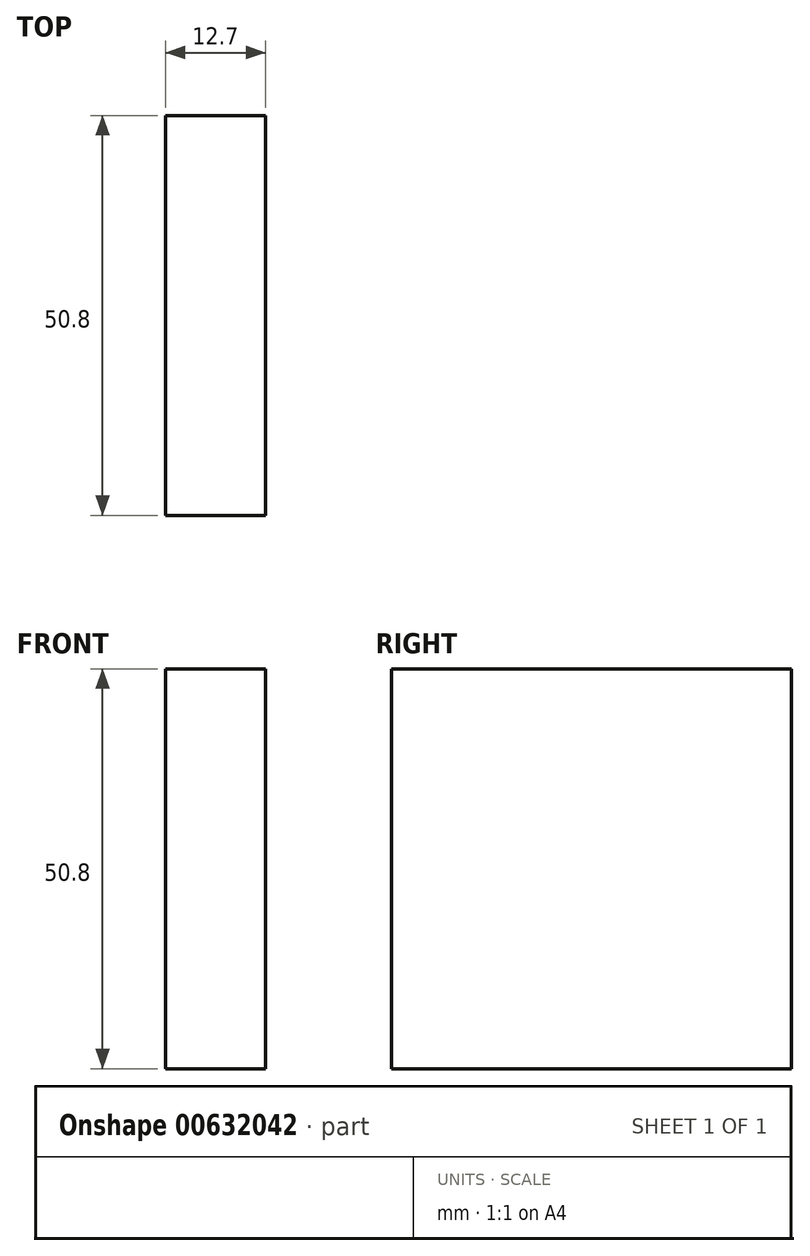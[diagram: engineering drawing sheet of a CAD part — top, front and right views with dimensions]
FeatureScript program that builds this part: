
annotation { "Feature Type Name" : "Feature", "Feature Type Description" : "" }
export const myFeature = defineFeature(function(context is Context, id is Id, definition is map)
    precondition{}
    {
        {
            var Q0;
            Q0=qCreatedBy(makeId("Front.planeOp"),FACE);
            var sketch = newSketch(context, id + "F0", { "sketchPlane" : qUnion([Q0])});
            skLineSegment(sketch, "E0.bottom", {"start": v(0, 0) * mm, "end": v(12.7, 0) * mm});
            skLineSegment(sketch, "E0.top", {"start": v(0, 50.8) * mm, "end": v(12.7, 50.8) * mm});
            skLineSegment(sketch, "E0.left", {"start": v(0, 0) * mm, "end": v(0, 50.8) * mm});
            skLineSegment(sketch, "E0.right", {"start": v(12.7, 0) * mm, "end": v(12.7, 50.8) * mm});
            skSolve(sketch);
        }
        {
            var Q0;
            Q0 = qSketchRegion(id + "F0", true);
            extrude(context, id + "F1", {"entities" : qUnion([Q0]), "depth" : 50.8 * mm, "offsetDistance" : 25.4 * mm});
        }
    });
